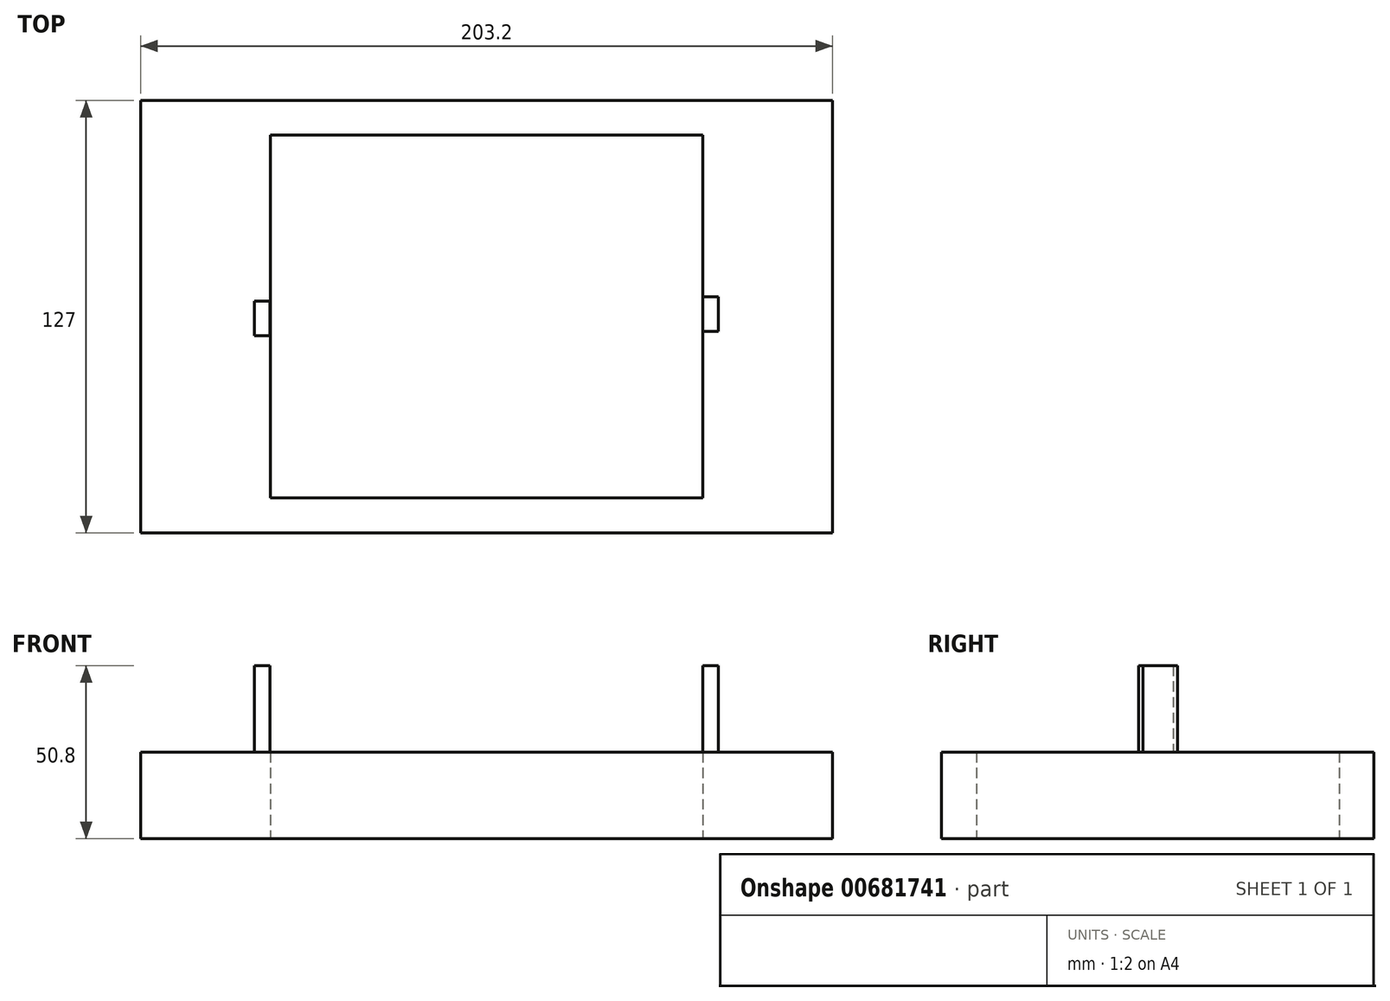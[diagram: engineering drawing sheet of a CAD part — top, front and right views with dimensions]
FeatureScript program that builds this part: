
annotation { "Feature Type Name" : "Feature", "Feature Type Description" : "" }
export const myFeature = defineFeature(function(context is Context, id is Id, definition is map)
    precondition{}
    {
        {
            var Q0;
            Q0=qCreatedBy(makeId("Top.planeOp"),FACE);
            var sketch = newSketch(context, id + "F0", { "sketchPlane" : qUnion([Q0])});
            skLineSegment(sketch, "E0.bottom", {"start": v(78.64, 63.83) * mm, "end": v(116.74, 63.83) * mm});
            skLineSegment(sketch, "E0.top", {"start": v(78.64, -63.17) * mm, "end": v(116.74, -63.17) * mm});
            skLineSegment(sketch, "E0.left", {"start": v(78.64, 63.83) * mm, "end": v(78.64, -63.17) * mm});
            skLineSegment(sketch, "E0.right", {"start": v(116.74, 63.83) * mm, "end": v(116.74, -63.17) * mm});
            skLineSegment(sketch, "E1.bottom", {"start": v(78.64, 63.83) * mm, "end": v(-48.36, 63.83) * mm});
            skLineSegment(sketch, "E1.top", {"start": v(78.64, 53.67) * mm, "end": v(-48.36, 53.67) * mm});
            skLineSegment(sketch, "E1.left", {"start": v(78.64, 63.83) * mm, "end": v(78.64, 53.67) * mm});
            skLineSegment(sketch, "E1.right", {"start": v(-48.36, 63.83) * mm, "end": v(-48.36, 53.67) * mm});
            skLineSegment(sketch, "E2.bottom", {"start": v(-48.36, 63.83) * mm, "end": v(-86.46, 63.83) * mm});
            skLineSegment(sketch, "E2.top", {"start": v(-48.36, -63.17) * mm, "end": v(-86.46, -63.17) * mm});
            skLineSegment(sketch, "E2.left", {"start": v(-48.36, 63.83) * mm, "end": v(-48.36, -63.17) * mm});
            skLineSegment(sketch, "E2.right", {"start": v(-86.46, 63.83) * mm, "end": v(-86.46, -63.17) * mm});
            skLineSegment(sketch, "E3.bottom", {"start": v(-48.36, -63.17) * mm, "end": v(78.64, -63.17) * mm});
            skLineSegment(sketch, "E3.top", {"start": v(-48.36, -52.89) * mm, "end": v(78.64, -52.89) * mm});
            skLineSegment(sketch, "E3.left", {"start": v(-48.36, -63.17) * mm, "end": v(-48.36, -52.89) * mm});
            skLineSegment(sketch, "E3.right", {"start": v(78.64, -63.17) * mm, "end": v(78.64, -52.89) * mm});
            skSolve(sketch);
        }
        {
            var Q0;
            Q0 = qSketchRegion(id + "F0", true);
            extrude(context, id + "F1", {"entities" : qUnion([Q0]), "depth" : 25.4 * mm, "offsetDistance" : 25.4 * mm});
        }
        {
            var Q0;
            Q0=qCreatedBy(makeId("Top.planeOp"),FACE);
            var sketch = newSketch(context, id + "F2", { "sketchPlane" : qUnion([Q0])});
            skLineSegment(sketch, "E4.bottom", {"start": v(-48.5, 4.87) * mm, "end": v(-53.07, 4.87) * mm});
            skLineSegment(sketch, "E4.top", {"start": v(-48.5, -5.29) * mm, "end": v(-53.07, -5.29) * mm});
            skLineSegment(sketch, "E4.left", {"start": v(-48.5, 4.87) * mm, "end": v(-48.5, -5.29) * mm});
            skLineSegment(sketch, "E4.right", {"start": v(-53.07, 4.87) * mm, "end": v(-53.07, -5.29) * mm});
            skSolve(sketch);
        }
        {
            var Q0;
            Q0 = qSketchRegion(id + "F2", true);
            extrude(context, id + "F3", {"entities" : qUnion([Q0]), "operationType" : NewBodyOperationType.ADD, "depth" : 50.8 * mm, "offsetDistance" : 25.4 * mm});
        }
        {
            var Q0;
            Q0=makeQuery(id+"F1.opExtrude","CAP_FACE",FACE,{"disambiguationData":[OSD([sQuery(id+"F0.wireOp",EDGE,"E0.bottom"),sQuery(id+"F0.wireOp",EDGE,"E0.top"),sQuery(id+"F0.wireOp",EDGE,"E0.left"),sQuery(id+"F0.wireOp",EDGE,"E0.right"),sQuery(id+"F0.wireOp",EDGE,"E1.bottom"),sQuery(id+"F0.wireOp",EDGE,"E1.top"),sQuery(id+"F0.wireOp",EDGE,"E2.bottom"),sQuery(id+"F0.wireOp",EDGE,"E2.top"),sQuery(id+"F0.wireOp",EDGE,"E2.left"),sQuery(id+"F0.wireOp",EDGE,"E2.right"),sQuery(id+"F0.wireOp",EDGE,"E3.bottom"),sQuery(id+"F0.wireOp",EDGE,"E3.top")])],"isStart":false});
            var sketch = newSketch(context, id + "F4", { "sketchPlane" : qUnion([Q0])});
            skLineSegment(sketch, "E5.bottom", {"start": v(78.64, 6.22) * mm, "end": v(83.21, 6.22) * mm});
            skLineSegment(sketch, "E5.top", {"start": v(78.64, -3.94) * mm, "end": v(83.21, -3.94) * mm});
            skLineSegment(sketch, "E5.left", {"start": v(78.64, 6.22) * mm, "end": v(78.64, -3.94) * mm});
            skLineSegment(sketch, "E5.right", {"start": v(83.21, 6.22) * mm, "end": v(83.21, -3.94) * mm});
            skSolve(sketch);
        }
        {
            var Q0;
            Q0 = qSketchRegion(id + "F4", true);
            extrude(context, id + "F5", {"entities" : qUnion([Q0]), "operationType" : NewBodyOperationType.ADD, "depth" : 25.4 * mm, "offsetDistance" : 25.4 * mm});
        }
    });
